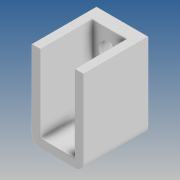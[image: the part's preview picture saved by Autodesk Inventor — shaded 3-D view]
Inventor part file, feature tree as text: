
AUTODESK INVENTOR PART (.ipt)
format: ipt  version: 2020 (Build 240168000, 168)  size: 228,864 bytes
history: native  units: mm
features: extrude x3, sketch x3, other x1, fillet x1
ambient origin geometry x8: Origin, YZ Plane, XZ Plane, XY Plane, X Axis, Y Axis, Z Axis, Center Point
bodies: Body1 (feature_tree)
feature tree (8):
  other  "솔리드1"
  extrude  "돌출1"  Depth=12.0mm
  extrude  "돌출2"  Depth=20.0mm
  extrude  "돌출3"  Depth=3.0mm TaperAngle=0.0deg
  fillet  "모깎기1"  Radius=2.0mm
  sketch  "스케치1"
  sketch  "스케치2"
  sketch  "스케치3"
